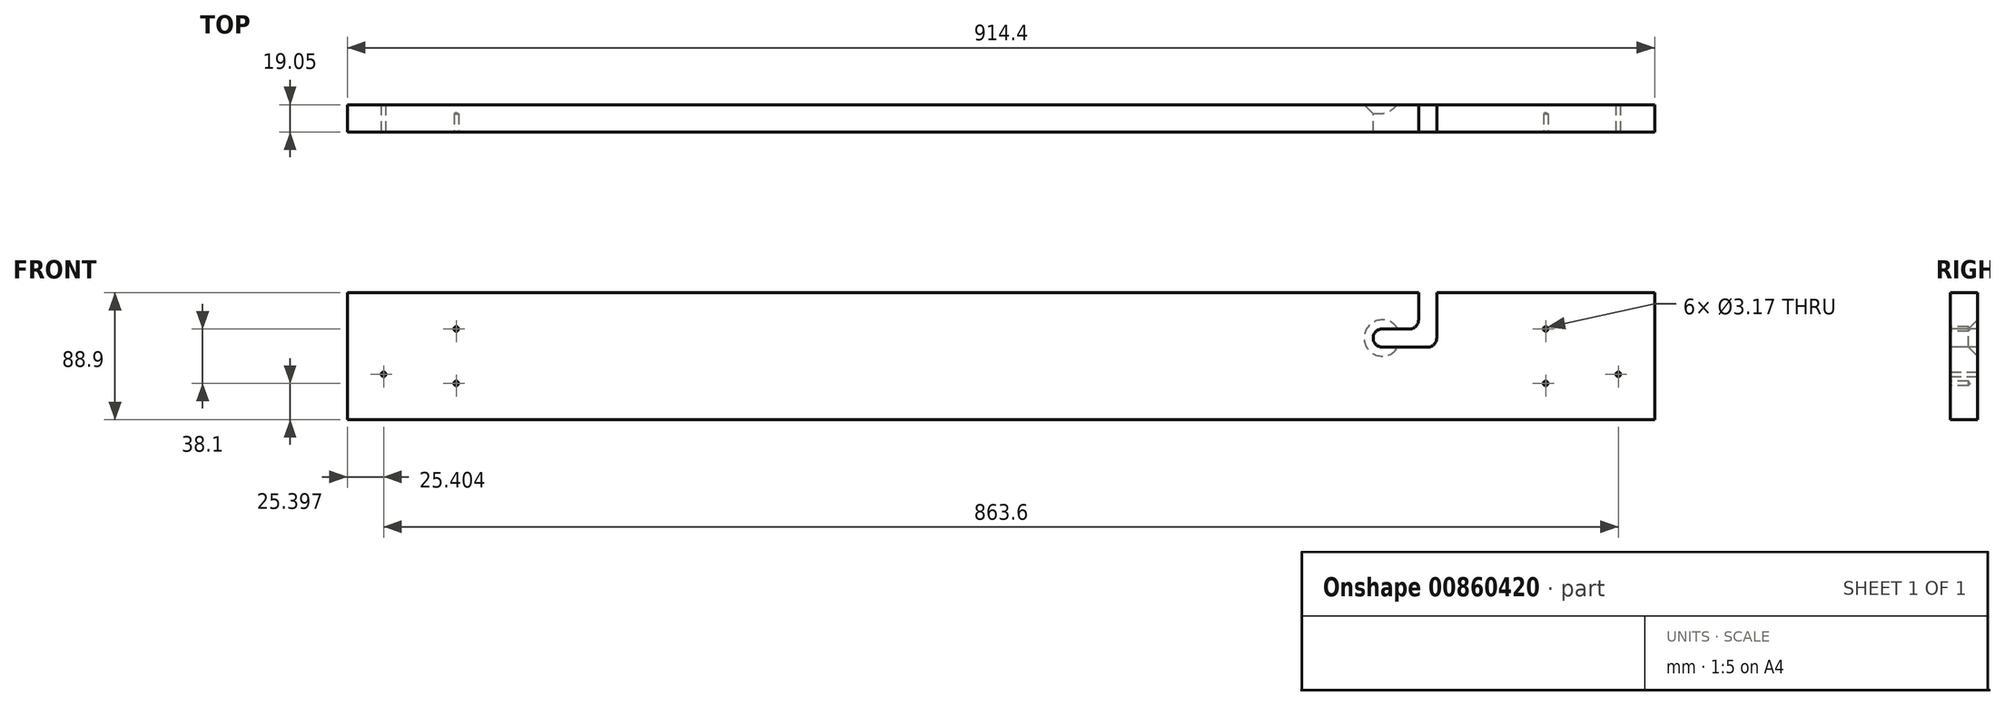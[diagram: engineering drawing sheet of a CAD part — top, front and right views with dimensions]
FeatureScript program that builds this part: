
annotation { "Feature Type Name" : "Feature", "Feature Type Description" : "" }
export const myFeature = defineFeature(function(context is Context, id is Id, definition is map)
    precondition{}
    {
        {
            var Q0;
            Q0=qCreatedBy(makeId("Front.planeOp"),FACE);
            var sketch = newSketch(context, id + "F0", { "sketchPlane" : qUnion([Q0])});
            skLineSegment(sketch, "E0.bottom", {"start": v(-564.38, 68.89) * mm, "end": v(350.02, 68.89) * mm});
            skLineSegment(sketch, "E0.top", {"start": v(-564.38, -20.01) * mm, "end": v(350.02, -20.01) * mm});
            skLineSegment(sketch, "E0.left", {"start": v(-564.38, 68.89) * mm, "end": v(-564.38, -20.01) * mm});
            skLineSegment(sketch, "E0.right", {"start": v(350.02, 68.89) * mm, "end": v(350.02, -20.01) * mm});
            skSolve(sketch);
        }
        {
            var Q0;
            Q0=makeQuery(id+"F0.imprint","IMPRINT",FACE,{"disambiguationData":[TD([[makeQuery(id+"F0.imprint","IMPRINT",EDGE,{"derivedFrom":sQuery(id+"F0.wireOp",EDGE,"E0.bottom")}),-1.0]])]});
            extrude(context, id + "F1", {"entities" : qUnion([Q0]), "depth" : 19.05 * mm, "offsetDistance" : 25.4 * mm});
        }
        {
            var Q0;
            Q0=makeQuery(id+"F1.opExtrude","CAP_FACE",FACE,{"disambiguationData":[OSD([sQuery(id+"F0.wireOp",EDGE,"E0.bottom"),sQuery(id+"F0.wireOp",EDGE,"E0.top"),sQuery(id+"F0.wireOp",EDGE,"E0.left"),sQuery(id+"F0.wireOp",EDGE,"E0.right")])],"isStart":false});
            var sketch = newSketch(context, id + "F2", { "sketchPlane" : qUnion([Q0])});
            skLineSegment(sketch, "E1", {"start": v(-488.18, 68.89) * mm, "end": v(-488.18, -20.01) * mm, "construction": true});
            skLineSegment(sketch, "E2", {"start": v(-107.18, 68.89) * mm, "end": v(-107.18, -20.01) * mm, "construction": true});
            skPoint(sketch, "E3", {"position": v(-488.18, 43.49) * mm});
            skPoint(sketch, "E4", {"position": v(-488.18, 5.39) * mm});
            skPoint(sketch, "E5.MirrorP", {"position": v(273.82, 43.49) * mm});
            skPoint(sketch, "E6.MirrorP", {"position": v(273.82, 5.39) * mm});
            skLineSegment(sketch, "E7", {"start": v(210.32, 68.89) * mm, "end": v(210.32, 49.84) * mm});
            skLineSegment(sketch, "E8", {"start": v(197.62, 68.89) * mm, "end": v(197.62, 37.14) * mm});
            skLineSegment(sketch, "E9", {"start": v(216.67, 43.49) * mm, "end": v(235.72, 43.49) * mm});
            skLineSegment(sketch, "E10", {"start": v(203.97, 30.79) * mm, "end": v(235.72, 30.79) * mm});
            skLineSegment(sketch, "E11", {"start": v(235.72, 43.49) * mm, "end": v(235.72, 30.79) * mm, "construction": true});
            skPoint(sketch, "E12.visualSharp", {"position": v(197.62, 30.79) * mm});
            skArc(sketch, "E12.filletArc", {"start": v(197.62, 37.14) * mm, "mid": v(199.48, 32.65) * mm, "end": v(203.97, 30.79) * mm});
            skPoint(sketch, "E13.visualSharp", {"position": v(210.32, 43.49) * mm});
            skArc(sketch, "E13.filletArc", {"start": v(210.32, 49.84) * mm, "mid": v(212.18, 45.35) * mm, "end": v(216.67, 43.49) * mm});
            skPoint(sketch, "E14.second.point", {"position": v(235.72, 45.91) * mm});
            skCircle(sketch, "E15", {"center": v(235.72, 37.14) * mm, "radius": 6.35 * mm});
            skLineSegment(sketch, "E16", {"start": v(210.32, 59.36) * mm, "end": v(197.62, 59.36) * mm, "construction": true});
            skLineSegment(sketch, "E17.MirrorCS", {"start": v(216.67, 18.09) * mm, "end": v(235.72, 18.09) * mm});
            skArc(sketch, "E18.MirrorCS", {"start": v(197.62, 37.14) * mm, "mid": v(195.76, 32.65) * mm, "end": v(191.27, 30.79) * mm});
            skArc(sketch, "E19.MirrorCS", {"start": v(184.92, 49.84) * mm, "mid": v(183.06, 45.35) * mm, "end": v(178.57, 43.49) * mm});
            skLineSegment(sketch, "E20.MirrorCS", {"start": v(184.92, 68.89) * mm, "end": v(184.92, 49.84) * mm});
            skCircle(sketch, "E21.MirrorC", {"center": v(159.52, 37.14) * mm, "radius": 6.35 * mm});
            skLineSegment(sketch, "E22.MirrorCS", {"start": v(178.57, 43.49) * mm, "end": v(159.52, 43.49) * mm});
            skLineSegment(sketch, "E23.MirrorCS", {"start": v(191.27, 30.79) * mm, "end": v(159.52, 30.79) * mm});
            skSolve(sketch);
        }
        {
            var Q0;
            Q0=sQuery(id+"F2.wireOp",VERTEX,"E5.MirrorP");
            var Q1;
            Q1=sQuery(id+"F2.wireOp",VERTEX,"E6.MirrorP");
            var Q2;
            Q2=sQuery(id+"F2.wireOp",VERTEX,"E3");
            var Q3;
            Q3=sQuery(id+"F2.wireOp",VERTEX,"E4");
            var Q4;
            Q4=makeQuery(id+"F1.opExtrude","SWEPT_BODY",BODY,{"disambiguationData":[OSD([sQuery(id+"F0.wireOp",EDGE,"E0.bottom"),sQuery(id+"F0.wireOp",EDGE,"E0.top"),sQuery(id+"F0.wireOp",EDGE,"E0.left"),sQuery(id+"F0.wireOp",EDGE,"E0.right")])]});
            hole(context, id + "F3", {"style" : HoleStyle.SIMPLE, "endStyle" : HoleEndStyle.BLIND, "holeDiameter" : 3.17 * mm, "majorDiameter" : 6.35 * mm, "holeDepth" : 12.7 * mm, "isTappedThrough" : true, "tappedDepth" : 12.7 * mm, "tapClearance" : 3, "locations" : qUnion([Q0, Q1, Q2, Q3]), "scope" : qUnion([Q4])});
        }
        {
            var Q0;
            {var subQ1=sQuery(id+"F2.wireOp",EDGE,"E8");Q0=makeQuery(id+"F2.imprint","IMPRINT",FACE,{"disambiguationData":[TD([[makeQuery(id+"F2.imprint","IMPRINT",EDGE,{"derivedFrom":subQ1}),-1.0]])]});}
            extrude(context, id + "F4", {"entities" : qUnion([Q0]), "operationType" : NewBodyOperationType.REMOVE, "endBound" : BoundingType.THROUGH_ALL, "oppositeDirection" : true, "depth" : 25.4 * mm, "offsetDistance" : 25.4 * mm});
        }
        {
            var Q0;
            Q0=makeQuery(id+"F1.opExtrude","CAP_FACE",FACE,{"disambiguationData":[OSD([sQuery(id+"F0.wireOp",EDGE,"E0.bottom"),sQuery(id+"F0.wireOp",EDGE,"E0.top"),sQuery(id+"F0.wireOp",EDGE,"E0.left"),sQuery(id+"F0.wireOp",EDGE,"E0.right")])],"isStart":true});
            var sketch = newSketch(context, id + "F5", { "sketchPlane" : qUnion([Q0])});
            skLineSegment(sketch, "E24", {"start": v(107.18, -20.01) * mm, "end": v(107.18, 68.89) * mm, "construction": true});
            skLineSegment(sketch, "E25", {"start": v(-324.62, 68.89) * mm, "end": v(-324.62, -20.01) * mm, "construction": true});
            skPoint(sketch, "E26", {"position": v(-324.62, 11.74) * mm});
            skLineSegment(sketch, "E27.MirrorCS", {"start": v(538.98, 68.89) * mm, "end": v(538.98, -20.01) * mm, "construction": true});
            skPoint(sketch, "E28.MirrorP", {"position": v(538.98, 11.74) * mm});
            skSolve(sketch);
        }
        {
            var Q0;
            Q0=sQuery(id+"F5.wireOp",VERTEX,"E26");
            var Q1;
            Q1=sQuery(id+"F5.wireOp",VERTEX,"E28.MirrorP");
            var Q2;
            Q2=makeQuery(id+"F1.opExtrude","SWEPT_BODY",BODY,{"disambiguationData":[OSD([sQuery(id+"F0.wireOp",EDGE,"E0.bottom"),sQuery(id+"F0.wireOp",EDGE,"E0.top"),sQuery(id+"F0.wireOp",EDGE,"E0.left"),sQuery(id+"F0.wireOp",EDGE,"E0.right")])]});
            hole(context, id + "F6", {"style" : HoleStyle.SIMPLE, "endStyle" : HoleEndStyle.THROUGH, "holeDiameter" : 3.17 * mm, "majorDiameter" : 6.35 * mm, "isTappedThrough" : true, "tappedDepth" : 12.7 * mm, "tapClearance" : 3, "locations" : qUnion([Q0, Q1]), "scope" : qUnion([Q2])});
        }
        {
            var Q0;
            Q0=makeQuery(id+"F1.opExtrude","CAP_FACE",FACE,{"disambiguationData":[OSD([sQuery(id+"F0.wireOp",EDGE,"E0.bottom"),sQuery(id+"F0.wireOp",EDGE,"E0.top"),sQuery(id+"F0.wireOp",EDGE,"E0.left"),sQuery(id+"F0.wireOp",EDGE,"E0.right")])],"isStart":true});
            var sketch = newSketch(context, id + "F7", { "sketchPlane" : qUnion([Q0])});
            skPoint(sketch, "E29", {"position": v(-432.14, 37.14) * mm});
            skPoint(sketch, "E30", {"position": v(-159.52, 37.14) * mm});
            skSolve(sketch);
        }
        {
            var Q0;
            Q0=sQuery(id+"F7.wireOp",VERTEX,"E30");
            var Q1;
            Q1=makeQuery(id+"F1.opExtrude","SWEPT_BODY",BODY,{"disambiguationData":[OSD([sQuery(id+"F0.wireOp",EDGE,"E0.bottom"),sQuery(id+"F0.wireOp",EDGE,"E0.top"),sQuery(id+"F0.wireOp",EDGE,"E0.left"),sQuery(id+"F0.wireOp",EDGE,"E0.right")])]});
            hole(context, id + "F8", {"style" : HoleStyle.C_SINK, "endStyle" : HoleEndStyle.THROUGH, "holeDiameter" : 12.7 * mm, "cSinkDiameter" : 25.4 * mm, "cSinkAngle" : 90 * degree, "majorDiameter" : 6.35 * mm, "isTappedThrough" : true, "tappedDepth" : 12.7 * mm, "tapClearance" : 3, "locations" : qUnion([Q0]), "scope" : qUnion([Q1])});
        }
    });
